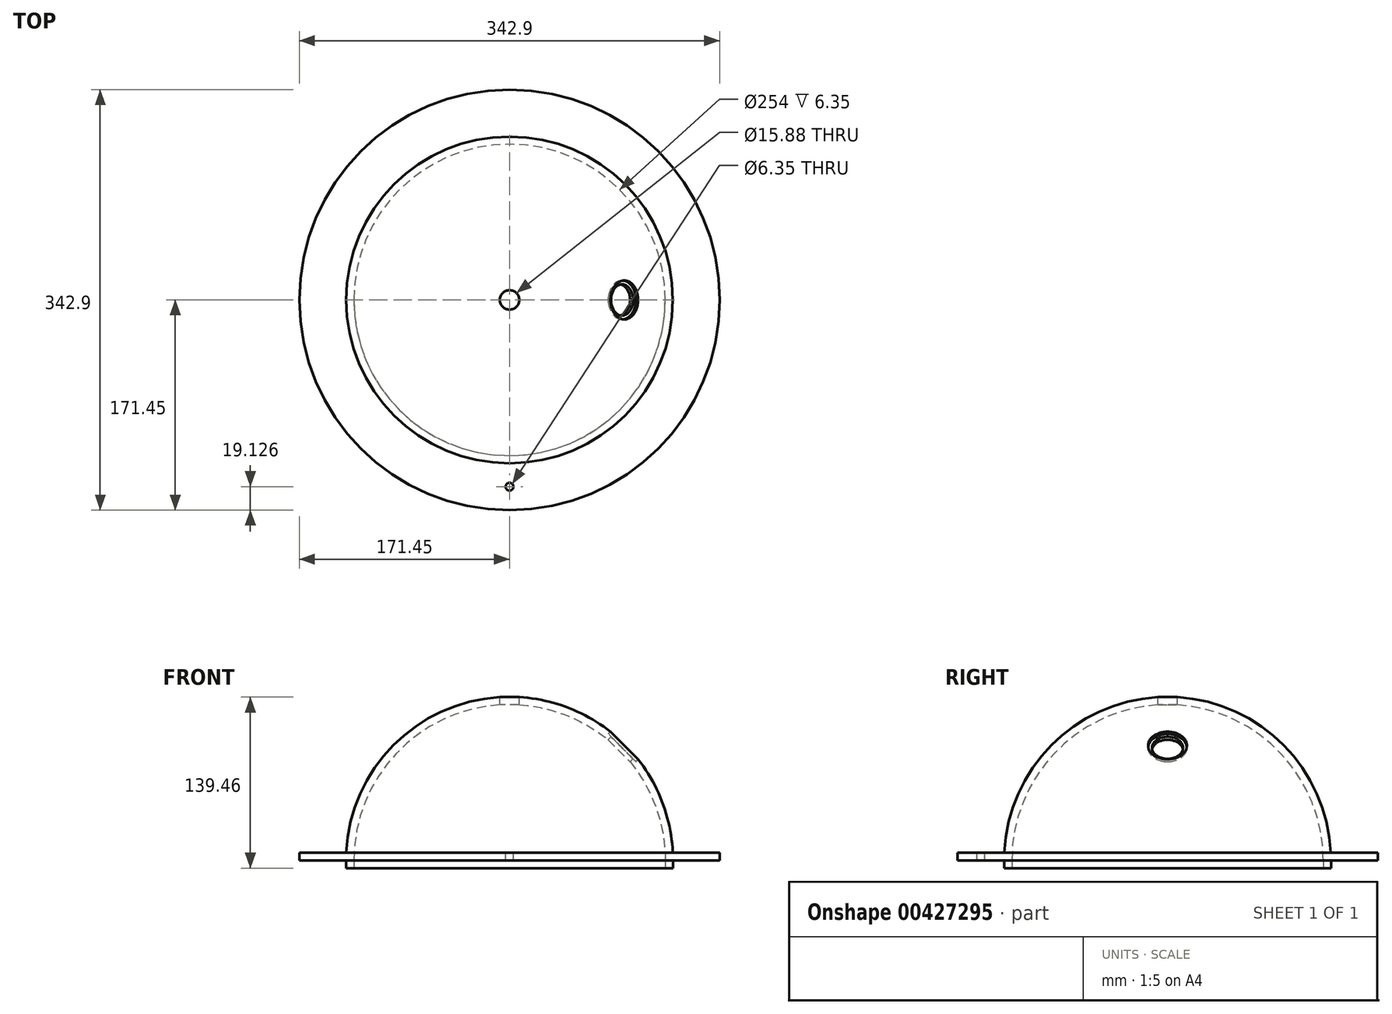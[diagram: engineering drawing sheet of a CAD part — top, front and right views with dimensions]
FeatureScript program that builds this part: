
annotation { "Feature Type Name" : "Feature", "Feature Type Description" : "" }
export const myFeature = defineFeature(function(context is Context, id is Id, definition is map)
    precondition{}
    {
        {
            var Q0;
            Q0=qCreatedBy(makeId("Front.planeOp"),FACE);
            var sketch = newSketch(context, id + "F0", { "sketchPlane" : qUnion([Q0])});
            skArc(sketch, "E0", {"start": v(127, 0) * mm, "mid": v(89.8, 89.8) * mm, "end": v(0, 127) * mm});
            skLineSegment(sketch, "E1", {"start": v(127, 0) * mm, "end": v(127, -6.35) * mm});
            skLineSegment(sketch, "E2", {"start": v(127, -6.35) * mm, "end": v(133.35, -6.35) * mm});
            skLineSegment(sketch, "E3", {"start": v(133.35, -6.35) * mm, "end": v(133.35, 0) * mm});
            skLineSegment(sketch, "E4", {"start": v(133.35, 0) * mm, "end": v(133.35, 0) * mm});
            skLineSegment(sketch, "E5", {"start": v(171.45, 6.35) * mm, "end": v(133.2, 6.35) * mm});
            skArc(sketch, "E6.0", {"start": v(133.2, 6.35) * mm, "mid": v(92.02, 96.51) * mm, "end": v(0, 133.35) * mm});
            skLineSegment(sketch, "E7", {"start": v(0, 127) * mm, "end": v(0, 133.35) * mm});
            skPoint(sketch, "E8.end.orphan", {"position": v(-133.35, 0) * mm});
            skLineSegment(sketch, "E9", {"start": v(0, 0) * mm, "end": v(0, 26.63) * mm, "construction": true});
            skLineSegment(sketch, "E10", {"start": v(133.35, 0) * mm, "end": v(171.45, 0) * mm});
            skLineSegment(sketch, "E11", {"start": v(171.45, 0) * mm, "end": v(171.45, 6.35) * mm});
            skSolve(sketch);
        }
        {
            var Q0;
            Q0=makeQuery(id+"F0.imprint","IMPRINT",FACE,{"disambiguationData":[TD([[makeQuery(id+"F0.imprint","IMPRINT",EDGE,{"derivedFrom":sQuery(id+"F0.wireOp",EDGE,"E0")}),-1.0]])]});
            var Q1;
            Q1=sQuery(id+"F0.wireOp",EDGE,"E9");
            revolve(context, id + "F1", {"entities" : qUnion([Q0]), "axis" : qUnion([Q1]), "revolveType" : RevolveType.FULL});
        }
        {
            var Q0;
            Q0=qCreatedBy(makeId("Front.planeOp"),FACE);
            var sketch = newSketch(context, id + "F2", { "sketchPlane" : qUnion([Q0])});
            skLineSegment(sketch, "E12", {"start": v(0, 0) * mm, "end": v(0, 155.52) * mm});
            skLineSegment(sketch, "E13", {"start": v(0, 0) * mm, "end": v(109.2, 109.2) * mm});
            skSolve(sketch);
        }
        {
            var Q0;
            Q0=qCreatedBy(makeId("Top.planeOp"),FACE);
            var Q1;
            Q1=sQuery(id+"F2.wireOp",EDGE,"E13");
            cPlane(context, id + "F3", {"entities" : qUnion([Q0, Q1]), "cplaneType" : CPlaneType.LINE_ANGLE, "offset" : 25.4 * mm, "angle" : 0 * degree, "oppositeDirection" : true, "width" : 152.4 * mm, "height" : 152.4 * mm});
        }
        {
            var Q0;
            Q0=qCreatedBy(makeId("Front.planeOp"),FACE);
            var sketch = newSketch(context, id + "F4", { "sketchPlane" : qUnion([Q0])});
            skArc(sketch, "E14", {"start": v(98.33, 80.37) * mm, "mid": v(94.19, 85.2) * mm, "end": v(89.8, 89.8) * mm});
            skLineSegment(sketch, "E15", {"start": v(89.8, 89.8) * mm, "end": v(94.3, 94.3) * mm});
            skLineSegment(sketch, "E16", {"start": v(0, 0) * mm, "end": v(0, 157.57) * mm});
            skLineSegment(sketch, "E17.0", {"start": v(98.33, 80.37) * mm, "end": v(100.78, 82.81) * mm});
            skLineSegment(sketch, "E18", {"start": v(103.02, 80.57) * mm, "end": v(100.78, 82.81) * mm});
            skLineSegment(sketch, "E19", {"start": v(103.02, 80.57) * mm, "end": v(110.36, 87.91) * mm});
            skPoint(sketch, "E20.trimOffspring.end.orphan", {"position": v(-133.2, 6.35) * mm});
            skPoint(sketch, "E21.trimOffspring.end.orphan", {"position": v(-127, 0) * mm});
            skPoint(sketch, "E22.start.orphan", {"position": v(133.2, 6.35) * mm});
            skLineSegment(sketch, "E23", {"start": v(94.3, 94.3) * mm, "end": v(110.36, 87.91) * mm});
            skPoint(sketch, "E24.orphan", {"position": v(127, 0) * mm});
            skSolve(sketch);
        }
        {
            var Q0;
            Q0=makeQuery(id+"F4.imprint","IMPRINT",FACE,{"disambiguationData":[TD([[makeQuery(id+"F4.imprint","IMPRINT",EDGE,{"derivedFrom":sQuery(id+"F4.wireOp",EDGE,"E14")}),-1.0]])]});
            var Q1;
            Q1=sQuery(id+"F4.wireOp",EDGE,"E15");
            revolve(context, id + "F5", {"operationType" : NewBodyOperationType.REMOVE, "entities" : qUnion([Q0]), "axis" : qUnion([Q1]), "revolveType" : RevolveType.FULL, "oppositeDirection" : true});
        }
        {
            var Q0;
            Q0=qCreatedBy(makeId("Front.planeOp"),FACE);
            var sketch = newSketch(context, id + "F6", { "sketchPlane" : qUnion([Q0])});
            skLineSegment(sketch, "E25", {"start": v(0, 127) * mm, "end": v(0, 133.35) * mm});
            skArc(sketch, "E26", {"start": v(0, 133.35) * mm, "mid": v(-3.97, 133.3) * mm, "end": v(-7.94, 133.11) * mm});
            skArc(sketch, "E27", {"start": v(-104.85, 82.4) * mm, "mid": v(-124.95, 46.58) * mm, "end": v(-133.2, 6.35) * mm});
            skArc(sketch, "E28", {"start": v(133.2, 6.35) * mm, "mid": v(124.95, 46.58) * mm, "end": v(104.85, 82.4) * mm});
            skArc(sketch, "E29", {"start": v(0, 127) * mm, "mid": v(-3.97, 126.94) * mm, "end": v(-7.94, 126.75) * mm});
            skArc(sketch, "E30", {"start": v(-98.33, 80.37) * mm, "mid": v(-119.62, 42.67) * mm, "end": v(-127, 0) * mm});
            skArc(sketch, "E31", {"start": v(127, 0) * mm, "mid": v(119.62, 42.67) * mm, "end": v(98.33, 80.37) * mm});
            skLineSegment(sketch, "E32.0", {"start": v(-7.94, 126.75) * mm, "end": v(-7.94, 133.11) * mm});
            skPoint(sketch, "E33.orphan", {"position": v(80.37, 98.33) * mm});
            skPoint(sketch, "E34.orphan", {"position": v(82.4, 104.85) * mm});
            skPoint(sketch, "E35.orphan", {"position": v(-82.4, 104.85) * mm});
            skPoint(sketch, "E36.orphan", {"position": v(-80.37, 98.33) * mm});
            skSolve(sketch);
        }
        {
            var Q0;
            Q0=makeQuery(id+"F6.imprint","IMPRINT",FACE,{"disambiguationData":[TD([[makeQuery(id+"F6.imprint","IMPRINT",EDGE,{"derivedFrom":sQuery(id+"F6.wireOp",EDGE,"E25")}),1.0]])]});
            var Q1;
            Q1=sQuery(id+"F6.wireOp",EDGE,"E25");
            revolve(context, id + "F7", {"operationType" : NewBodyOperationType.REMOVE, "entities" : qUnion([Q0]), "axis" : qUnion([Q1]), "revolveType" : RevolveType.FULL, "oppositeDirection" : true});
        }
        {
            var Q0;
            Q0=makeQuery(id+"F1.opRevolve","SWEPT_FACE",FACE,{"disambiguationData":[OSD([sQuery(id+"F0.wireOp",EDGE,"E5")])]});
            var sketch = newSketch(context, id + "F8", { "sketchPlane" : qUnion([Q0])});
            skLineSegment(sketch, "E37", {"start": v(0, -133.2) * mm, "end": v(0, -171.45) * mm, "construction": true});
            skCircle(sketch, "E38", {"center": v(0, 0) * mm, "radius": 171.45 * mm, "construction": true});
            skCircle(sketch, "E39", {"center": v(0, 0) * mm, "radius": 133.2 * mm, "construction": true});
            skPoint(sketch, "E40", {"position": v(0, -152.32) * mm});
            skSolve(sketch);
        }
        {
            var Q0;
            Q0=sQuery(id+"F8.wireOp",VERTEX,"E40");
            var Q1;
            Q1=makeQuery(id+"F1.opRevolve","SWEPT_BODY",BODY,{"disambiguationData":[OSD([sQuery(id+"F0.wireOp",EDGE,"E0"),sQuery(id+"F0.wireOp",EDGE,"E1"),sQuery(id+"F0.wireOp",EDGE,"E2"),sQuery(id+"F0.wireOp",EDGE,"E3"),sQuery(id+"F0.wireOp",EDGE,"E5"),sQuery(id+"F0.wireOp",EDGE,"E6.0"),sQuery(id+"F0.wireOp",EDGE,"E7"),sQuery(id+"F0.wireOp",EDGE,"E10"),sQuery(id+"F0.wireOp",EDGE,"E11")])]});
            hole(context, id + "F9", {"style" : HoleStyle.SIMPLE, "endStyle" : HoleEndStyle.THROUGH, "holeDiameter" : 6.35 * mm, "isTappedThrough" : true, "tappedDepth" : 12.7 * mm, "tapClearance" : 3, "locations" : qUnion([Q0]), "scope" : qUnion([Q1])});
        }
    });
